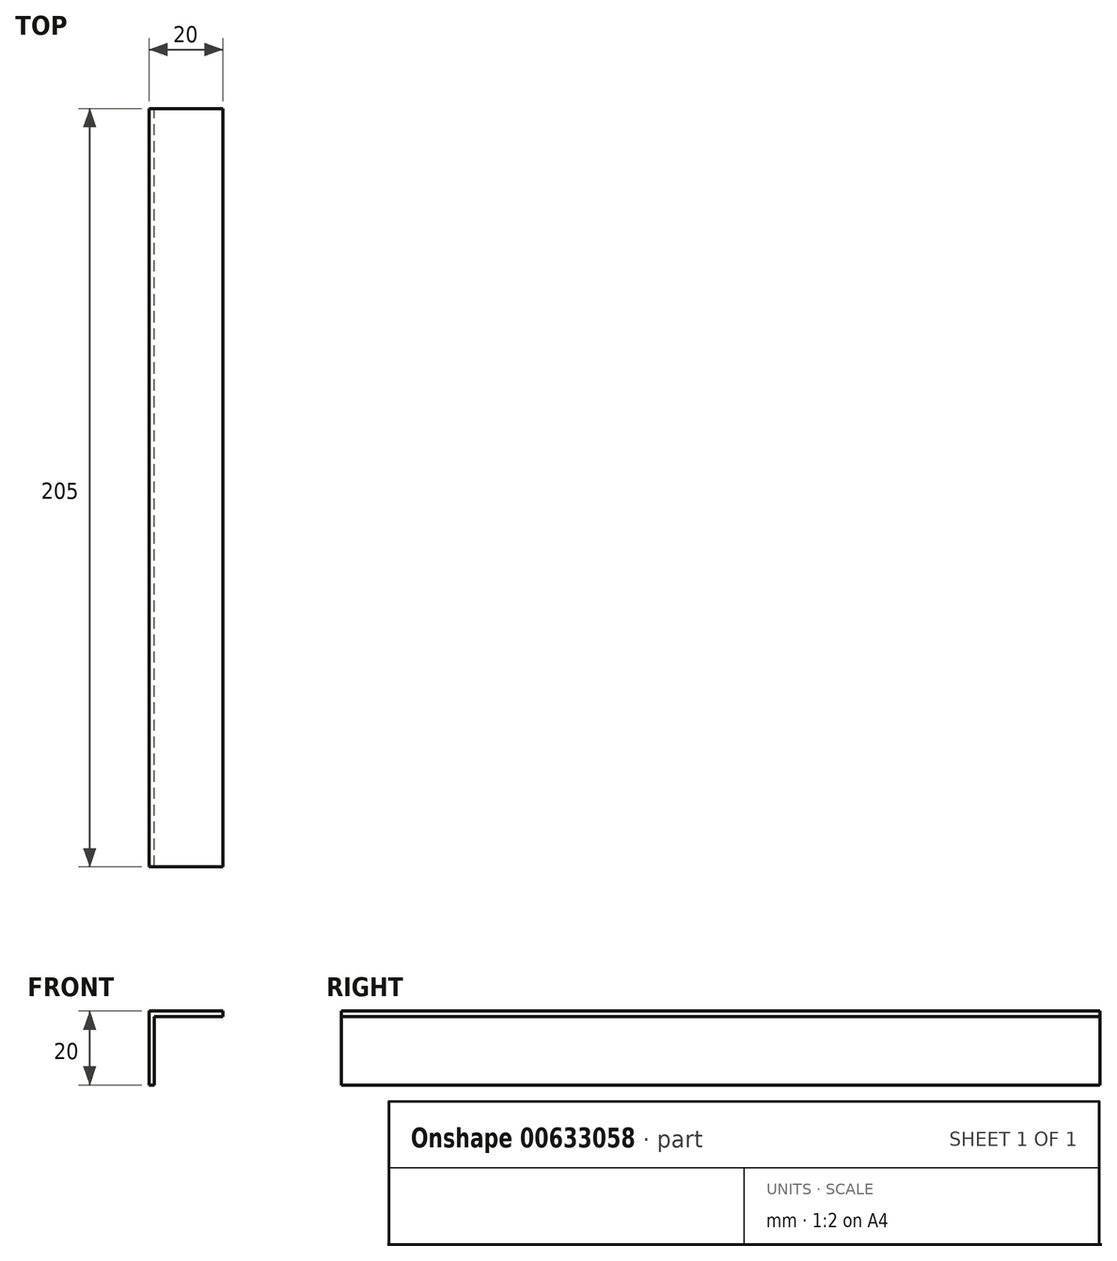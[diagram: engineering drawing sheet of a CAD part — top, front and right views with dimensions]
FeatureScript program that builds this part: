
annotation { "Feature Type Name" : "Feature", "Feature Type Description" : "" }
export const myFeature = defineFeature(function(context is Context, id is Id, definition is map)
    precondition{}
    {
        {
            var Q0;
            Q0=qCreatedBy(makeId("Front.planeOp"),FACE);
            var sketch = newSketch(context, id + "F0", { "sketchPlane" : qUnion([Q0])});
            skLineSegment(sketch, "E0", {"start": v(20, 0) * mm, "end": v(0, 0) * mm});
            skLineSegment(sketch, "E1", {"start": v(0, 0) * mm, "end": v(0, -20) * mm});
            skLineSegment(sketch, "E2", {"start": v(0, -20) * mm, "end": v(1.5, -20) * mm});
            skLineSegment(sketch, "E3", {"start": v(1.5, -20) * mm, "end": v(1.5, -1.5) * mm});
            skLineSegment(sketch, "E4", {"start": v(1.5, -1.5) * mm, "end": v(20, -1.5) * mm});
            skLineSegment(sketch, "E5", {"start": v(20, -1.5) * mm, "end": v(20, 0) * mm});
            skSolve(sketch);
        }
        {
            var Q0;
            Q0=makeQuery(id+"F0.imprint","IMPRINT",FACE,{"disambiguationData":[TD([[makeQuery(id+"F0.imprint","IMPRINT",EDGE,{"derivedFrom":sQuery(id+"F0.wireOp",EDGE,"E0")}),1.0]])]});
            extrude(context, id + "F1", {"entities" : qUnion([Q0]), "depth" : 205 * mm, "offsetDistance" : 25 * mm});
        }
    });
